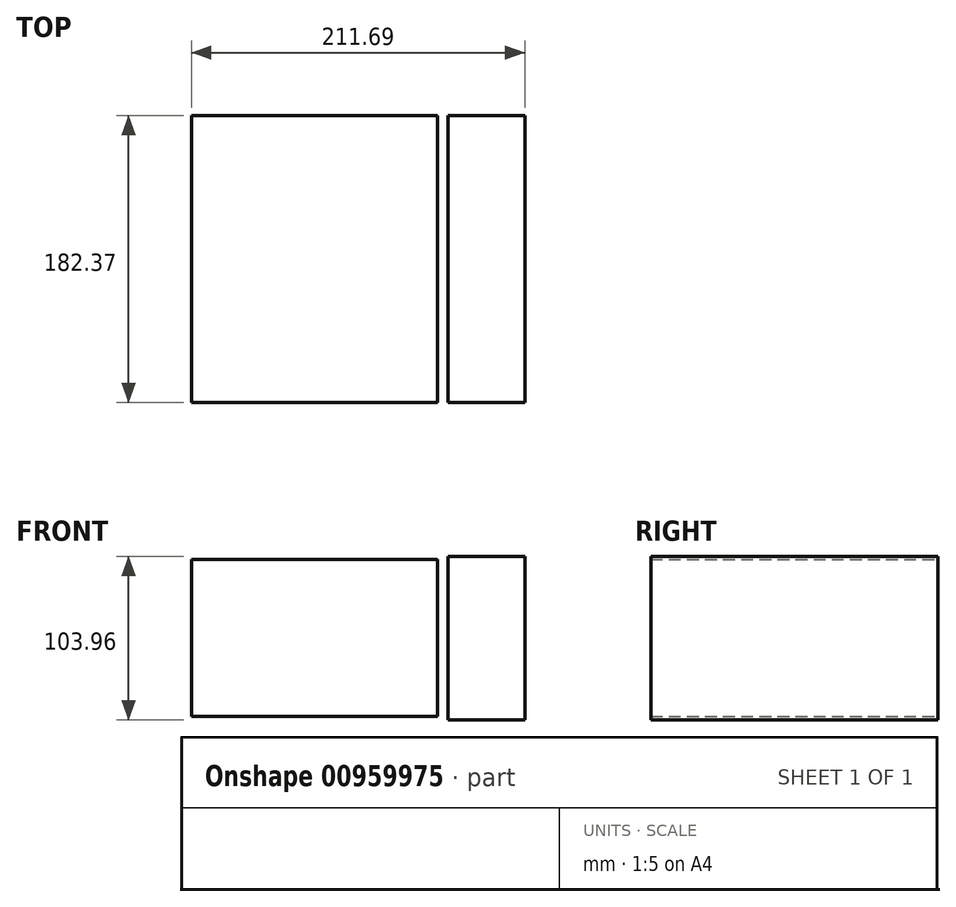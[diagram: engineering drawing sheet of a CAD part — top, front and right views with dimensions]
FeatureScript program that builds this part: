
annotation { "Feature Type Name" : "Feature", "Feature Type Description" : "" }
export const myFeature = defineFeature(function(context is Context, id is Id, definition is map)
    precondition{}
    {
        {
            var Q0;
            Q0=qCreatedBy(makeId("Front.planeOp"),FACE);
            var sketch = newSketch(context, id + "F0", { "sketchPlane" : qUnion([Q0])});
            skLineSegment(sketch, "E0.bottom", {"start": v(-93.42, 14.96) * mm, "end": v(62.89, 14.96) * mm});
            skLineSegment(sketch, "E0.top", {"start": v(-93.42, -84.85) * mm, "end": v(62.89, -84.85) * mm});
            skLineSegment(sketch, "E0.left", {"start": v(-93.42, 14.96) * mm, "end": v(-93.42, -84.85) * mm});
            skLineSegment(sketch, "E0.right", {"start": v(62.89, 14.96) * mm, "end": v(62.89, -84.85) * mm});
            skLineSegment(sketch, "E1.bottom", {"start": v(69.62, 17) * mm, "end": v(118.27, 17) * mm});
            skLineSegment(sketch, "E1.top", {"start": v(69.62, -86.97) * mm, "end": v(118.27, -86.97) * mm});
            skLineSegment(sketch, "E1.left", {"start": v(69.62, 17) * mm, "end": v(69.62, -86.97) * mm});
            skLineSegment(sketch, "E1.right", {"start": v(118.27, 17) * mm, "end": v(118.27, -86.97) * mm});
            skSolve(sketch);
        }
        {
            var Q0;
            Q0=makeQuery(id+"F0.imprint","IMPRINT",FACE,{"disambiguationData":[TD([[makeQuery(id+"F0.imprint","IMPRINT",EDGE,{"derivedFrom":sQuery(id+"F0.wireOp",EDGE,"E0.bottom")}),-1.0]])]});
            var Q1;
            Q1=makeQuery(id+"F0.imprint","IMPRINT",FACE,{"disambiguationData":[TD([[makeQuery(id+"F0.imprint","IMPRINT",EDGE,{"derivedFrom":sQuery(id+"F0.wireOp",EDGE,"E1.bottom")}),-1.0]])]});
            extrude(context, id + "F1", {"entities" : qUnion([Q0, Q1]), "depth" : 182.37 * mm, "offsetDistance" : 25.4 * mm});
        }
    });
